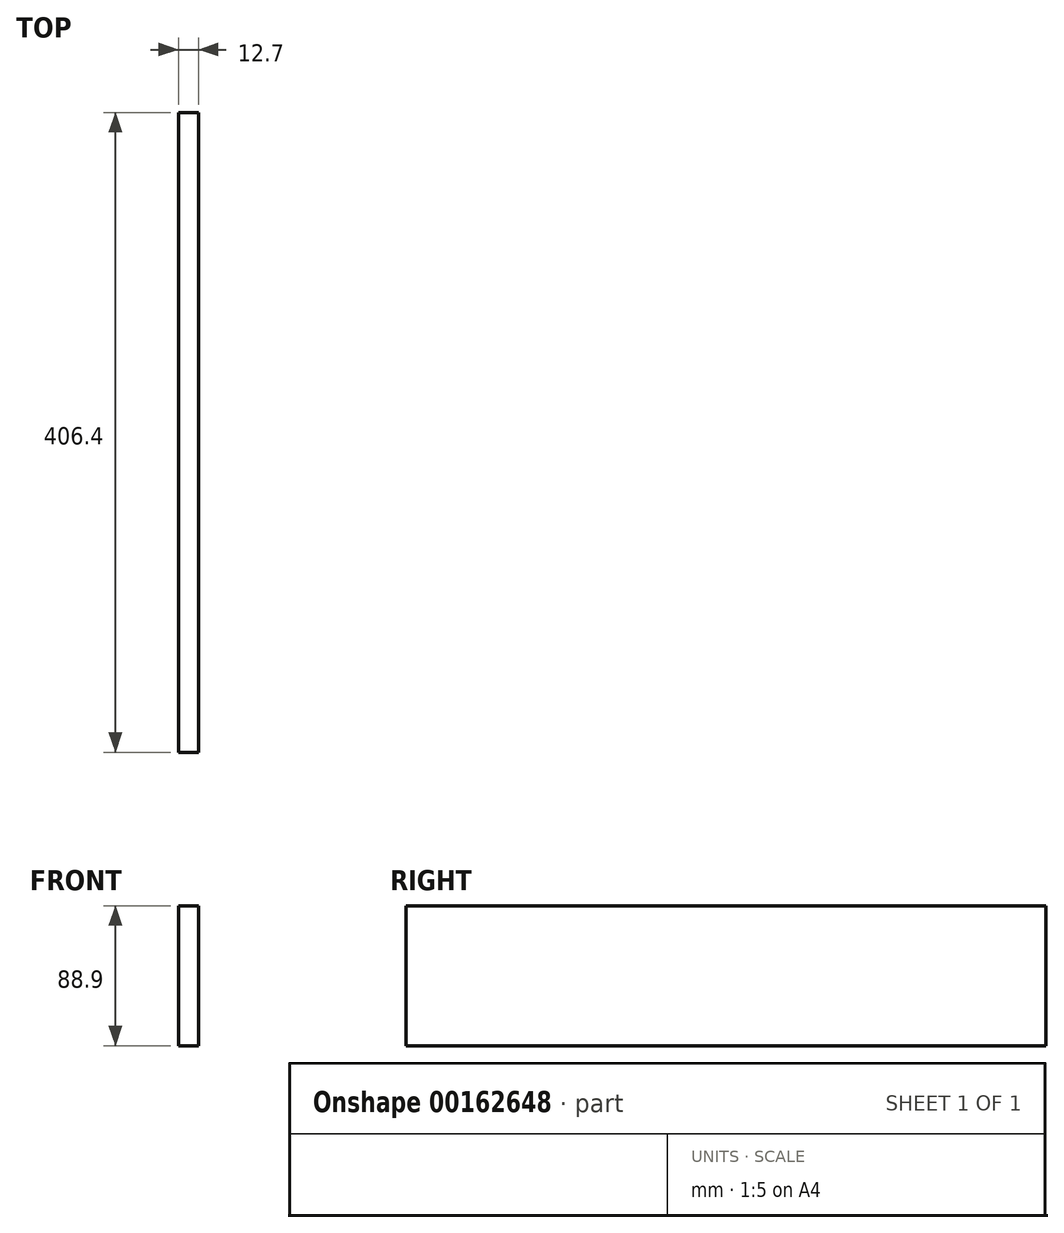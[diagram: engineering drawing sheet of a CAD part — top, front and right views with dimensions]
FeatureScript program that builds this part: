
annotation { "Feature Type Name" : "Feature", "Feature Type Description" : "" }
export const myFeature = defineFeature(function(context is Context, id is Id, definition is map)
    precondition{}
    {
        {
            var Q0;
            Q0=qCreatedBy(makeId("Right.planeOp"),FACE);
            var sketch = newSketch(context, id + "F0", { "sketchPlane" : qUnion([Q0])});
            skLineSegment(sketch, "E0.bottom", {"start": v(-214.83, 78.18) * mm, "end": v(191.57, 78.18) * mm});
            skLineSegment(sketch, "E0.top", {"start": v(-214.83, -10.72) * mm, "end": v(191.57, -10.72) * mm});
            skLineSegment(sketch, "E0.left", {"start": v(-214.83, 78.18) * mm, "end": v(-214.83, -10.72) * mm});
            skLineSegment(sketch, "E0.right", {"start": v(191.57, 78.18) * mm, "end": v(191.57, -10.72) * mm});
            skSolve(sketch);
        }
        {
            var Q0;
            Q0 = qSketchRegion(id + "F0", true);
            extrude(context, id + "F1", {"entities" : qUnion([Q0]), "depth" : 12.7 * mm});
        }
    });
